# Revit family: Legrand_Lighting_Management_Standalone_Presence_Sensor_Ceiling_R2
name_source: partatom
category: Dispositifs d'éclairage
units: mm (PartAtom-declared; Revit-internal decimal feet)

## family parameters
Conserver l'orientation des annotations = Non
Cote de connecteur circulaire = Utiliser le diamètre
Couper avec des vides une fois chargée = Non
Hôte = Face
Partagée = Non
Point de calcul de pièce = Non
Type d'élément = Normal

## types (16) — shared parameters
COULOIR_PIR = INTERDETECTEUR_COULOIR_PIR
Color = White
Constant light control = Oui
DOUBLE_TECHNO = INTERDETECTEUR_DOUBLE-TECHNO_RACC_VIS
Elévation par défaut = 1219 mm
FAUX_PLAFOND_PIR = DETECTEUR_FAUX_PLAFOND_PIR
Fabricant = LEGRAND
General Conditions of Use = https://export.legrand.com
IP55 = ECODETECTEUR_IP55_ECO_2_GRANDE_HAUTEUR
IR_360 = INTERDETECTEUR_IR_360
IR_360_45_M_2 = INTERDETECTEUR_IR_360_45_M_2
Installation method = Fluxh-mounting
MW_FAUX_PLAFOND = DETECTEUR_MW_FAUX_PLAFOND
PIR_COMPACT = DETECTEUR_PIR_COMPACT
PIR_MID_RANGE = DETECTEUR_PIR_MID_RANGE
PIR_MINI = DETECTEUR_PIR_MINI
Response value luminosity adjustable = Oui
Response value sensitivity adjustable = Oui
URL = www.legrand.fr

## per-type parameters (varying)
- MID RANGE-IR - 360° - 1-10V: DETECTEUR=DETECTEUR_PIR_MID_RANGE; Depth=77 mm  [stored 0.252625 ft]; Detection angle horizontal=360-360 °; Diameter=76 mm  [stored 0.249344 ft]; Diameter detection range on floor=15000 mm  [stored 49.2126 ft]; Frequency=50 Hz; HVAC-control=Non; Height=0 mm  [stored 0 ft]; IK=05; IP=40; Max. duty cycle=99; Max. starting current=80 A; Max. switching power=2300 W; Max. transmission range frontally=7500 mm  [stored 24.6063 ft]; Max. transmission range sideways=7500 mm  [stored 24.6063 ft]; Min. switch-on time=0.5; Operating temperature MIN-MAX=-10/+30 °C; Optimum mounting height=2800 mm  [stored 9.18635 ft]; PETITE_ZONE=Non; Power supply=230 AC; Product Model=presence sensor; Product designation=DETECTOR PIR MID RANGE DIMMING 1-10V & SWITCHING; Reference=LG-048969; Remote operation=Oui; Response value luminosity=0-2000 lx; Sensor type=infrared; Substation input=Oui; Suitable for wireless transmission=Non; Width=76 mm  [stored 0.249344 ft]; With alarm function=Non; With remote control=Oui
- MID RANGE-IR - 360° - DALI: DETECTEUR=DETECTEUR_PIR_MID_RANGE; Depth=77 mm  [stored 0.252625 ft]; Detection angle horizontal=360-360 °; Diameter=76 mm  [stored 0.249344 ft]; Diameter detection range on floor=15000 mm  [stored 49.2126 ft]; Frequency=50 Hz; HVAC-control=Non; Height=0 mm  [stored 0 ft]; IK=05; IP=40; Max. duty cycle=99; Max. starting current=80 A; Max. switching power=2300 W; Max. transmission range frontally=7500 mm  [stored 24.6063 ft]; Max. transmission range sideways=7500 mm  [stored 24.6063 ft]; Min. switch-on time=0.5; Operating temperature MIN-MAX=-10/+30 °C; Optimum mounting height=2800 mm  [stored 9.18635 ft]; PETITE_ZONE=Non; Power supply=230 AC; Product Model=presence sensor; Product designation=DETECTOR PIR MID RANGE DIMMING DALI & SWITCHING; Reference=LG-048968; Remote operation=Oui; Response value luminosity=0-2000 lx; Sensor type=infrared; Substation input=Oui; Suitable for wireless transmission=Non; Width=76 mm  [stored 0.249344 ft]; With alarm function=Non; With remote control=Oui
- MID RANGE-IR - 360° - 2 Chanels: DETECTEUR=DETECTEUR_PIR_MID_RANGE; Depth=70 mm; Detection angle horizontal=360-360 °; Diameter=76 mm  [stored 0.249344 ft]; Diameter detection range on floor=15000 mm  [stored 49.2126 ft]; Frequency=50 Hz; HVAC-control=Non; Height=0 mm  [stored 0 ft]; IK=05; IP=40; Max. duty cycle=99; Max. starting current=80 A; Max. switching power=1300 W; Max. transmission range frontally=7500 mm  [stored 24.6063 ft]; Max. transmission range sideways=7500 mm  [stored 24.6063 ft]; Min. switch-on time=0.5; Operating temperature MIN-MAX=-10/+30 °C; Optimum mounting height=2800 mm  [stored 9.18635 ft]; PETITE_ZONE=Non; Power supply=230 AC; Product Model=presence sensor; Product designation=DETECTOR PIR MID RANGE SWITCHING 2 CHANNELS; Reference=LG-048970; Remote operation=Oui; Response value luminosity=0-2000 lx; Sensor type=infrared; Substation input=Oui; Suitable for wireless transmission=Non; Width=76 mm  [stored 0.249344 ft]; With alarm function=Non; With remote control=Oui
- MINI-IR - 360° - 1-10V: DETECTEUR=DETECTEUR_PIR_MINI; Depth=30 mm  [stored 0.0984252 ft]; Detection angle horizontal=360-360 °; Diameter=28 mm  [stored 0.0918635 ft]; Diameter detection range on floor=7000 mm  [stored 22.9659 ft]; Frequency=50 Hz; HVAC-control=Non; Height=0 mm  [stored 0 ft]; IK=05; IP=40; Max. duty cycle=99; Max. starting current=80 A; Max. switching power=1300 W; Max. transmission range frontally=3500 mm  [stored 11.4829 ft]; Max. transmission range sideways=3500 mm  [stored 11.4829 ft]; Min. switch-on time=0.5; Operating temperature MIN-MAX=-10/+30 °C; Optimum mounting height=2800 mm  [stored 9.18635 ft]; PETITE_ZONE=Oui; Power supply=230 AC; Product Model=presence sensor; Product designation=DETECTOR PIR MINIATURE DIMMING 1-10V & SWITCHING; Reference=LG-048966; Remote operation=Oui; Response value luminosity=0-2000 lx; Sensor type=infrared; Substation input=Oui; Suitable for wireless transmission=Non; Width=76 mm  [stored 0.249344 ft]; With alarm function=Non; With remote control=Oui
- MINI-IR - 360° - DALI: DETECTEUR=DETECTEUR_PIR_MINI; Depth=30 mm  [stored 0.0984252 ft]; Detection angle horizontal=360-360 °; Diameter=0 mm  [stored 0 ft]; Diameter detection range on floor=7000 mm  [stored 22.9659 ft]; Frequency=50 Hz; HVAC-control=Non; Height=33 mm  [stored 0.108268 ft]; IK=05; IP=40; Max. duty cycle=0.1; Max. starting current=80 A; Max. switching power=2400 W; Max. transmission range frontally=7000 mm  [stored 22.9659 ft]; Max. transmission range sideways=7000 mm  [stored 22.9659 ft]; Min. switch-on time=1; Operating temperature MIN-MAX=-10/+35 °C; Optimum mounting height=2800 mm  [stored 9.18635 ft]; PETITE_ZONE=Non; Power supply=230 AC; Product Model=other; Product designation=PIR MINI FALSE CEILING SENSOR DALI DIMMING; Reference=LG-048953; Remote operation=Oui; Response value luminosity=0-2000 lx; Sensor type=infrared; Substation input=Oui; Suitable for wireless transmission=Non; Width=28 mm  [stored 0.0918635 ft]; With alarm function=Non; With remote control=Oui
- MINI-IR - 360° - ON-OFF: DETECTEUR=DETECTEUR_PIR_MINI; Depth=30 mm  [stored 0.0984252 ft]; Detection angle horizontal=360-360 °; Diameter=0 mm  [stored 0 ft]; Diameter detection range on floor=7000 mm  [stored 22.9659 ft]; Frequency=50 Hz; HVAC-control=Non; Height=33 mm  [stored 0.108268 ft]; IK=05; IP=40; Max. duty cycle=0.1; Max. starting current=80 A; Max. switching power=2400 W; Max. transmission range frontally=7000 mm  [stored 22.9659 ft]; Max. transmission range sideways=7000 mm  [stored 22.9659 ft]; Min. switch-on time=1; Operating temperature MIN-MAX=-10/+35 °C; Optimum mounting height=2800 mm  [stored 9.18635 ft]; PETITE_ZONE=Non; Power supply=230 AC; Product Model=other; Product designation=PIR MINI FALSE CEILING SENSOR ON-OFF; Reference=LG-048954; Remote operation=Oui; Response value luminosity=0-2000 lx; Sensor type=infrared; Substation input=Oui; Suitable for wireless transmission=Non; Width=28 mm  [stored 0.0918635 ft]; With alarm function=Non; With remote control=Oui
- COMPACT-IR - 360° - 12-48V: DETECTEUR=DETECTEUR_PIR_COMPACT; Depth=70 mm; Detection angle horizontal=360-360 °; Diameter=0 mm  [stored 0 ft]; Diameter detection range on floor=7000 mm  [stored 22.9659 ft]; Frequency=50 Hz; HVAC-control=Non; Height=65 mm  [stored 0.213255 ft]; IK=05; IP=40; Max. duty cycle=0.1; Max. starting current=80 A; Max. switching power=2400 W; Max. transmission range frontally=7000 mm  [stored 22.9659 ft]; Max. transmission range sideways=7000 mm  [stored 22.9659 ft]; Min. switch-on time=1; Operating temperature MIN-MAX=-10/+35 °C; Optimum mounting height=2800 mm  [stored 9.18635 ft]; PETITE_ZONE=Non; Power supply=24 AC/DC; Product Model=other; Product designation=PIR FALSE CEILING SENSOR LOW VOLTAGE 12-48V SUPPLIED; Reference=LG-048952; Remote operation=Oui; Response value luminosity=0-2000 lx; Sensor type=infrared; Substation input=Oui; Suitable for wireless transmission=Non; Width=76 mm  [stored 0.249344 ft]; With alarm function=Non; With remote control=Oui
- COMPACT-IR - 360° - DALI: DETECTEUR=DETECTEUR_PIR_COMPACT; Depth=70 mm; Detection angle horizontal=360-360 °; Diameter=76 mm  [stored 0.249344 ft]; Diameter detection range on floor=7000 mm  [stored 22.9659 ft]; Frequency=50 Hz; HVAC-control=Non; Height=0 mm  [stored 0 ft]; IK=05; IP=40; Max. duty cycle=99; Max. starting current=80 A; Max. switching power=2300 W; Max. transmission range frontally=3500 mm  [stored 11.4829 ft]; Max. transmission range sideways=3500 mm  [stored 11.4829 ft]; Min. switch-on time=0.5; Operating temperature MIN-MAX=-10/+30 °C; Optimum mounting height=2800 mm  [stored 9.18635 ft]; PETITE_ZONE=Oui; Power supply=230 AC; Product Model=presence sensor; Product designation=DETECTOR PIR COMPACT DIMMING DALI & SWITCHING; Reference=LG-048964; Remote operation=Oui; Response value luminosity=0-2000 lx; Sensor type=infrared; Substation input=Oui; Suitable for wireless transmission=Non; Width=76 mm  [stored 0.249344 ft]; With alarm function=Non; With remote control=Oui
- COMPACT-IR - 360° - 1-10V: DETECTEUR=DETECTEUR_PIR_COMPACT; Depth=70 mm; Detection angle horizontal=360-360 °; Diameter=20 mm  [stored 0.0656168 ft]; Diameter detection range on floor=7000 mm  [stored 22.9659 ft]; Frequency=50 Hz; HVAC-control=Non; Height=0 mm  [stored 0 ft]; IK=05; IP=40; Max. duty cycle=99; Max. starting current=80 A; Max. switching power=2300 W; Max. transmission range frontally=3500 mm  [stored 11.4829 ft]; Max. transmission range sideways=3500 mm  [stored 11.4829 ft]; Min. switch-on time=0.5; Operating temperature MIN-MAX=-10/+30 °C; Optimum mounting height=2800 mm  [stored 9.18635 ft]; PETITE_ZONE=Oui; Power supply=230 AC; Product Model=presence sensor; Product designation=DETECTOR PIR COMPACT DIMMING 1-10V & SWITCHING; Reference=LG-048965; Remote operation=Oui; Response value luminosity=0-2000 lx; Sensor type=infrared; Substation input=Oui; Suitable for wireless transmission=Non; Width=76 mm  [stored 0.249344 ft]; With alarm function=Non; With remote control=Oui
- MW-DALI-Adjustable head: DETECTEUR=DETECTEUR_MW_FAUX_PLAFOND; Depth=99 mm  [stored 0.324803 ft]; Detection angle horizontal=180-360 °; Diameter=0 mm  [stored 0 ft]; Diameter detection range on floor=22000 mm  [stored 72.1785 ft]; Frequency=50 Hz; HVAC-control=Non; Height=96 mm; IK=05; IP=40; Max. duty cycle=0.1; Max. starting current=80 A; Max. switching power=2400 W; Max. transmission range frontally=30000 mm  [stored 98.4252 ft]; Max. transmission range sideways=6000 mm  [stored 19.685 ft]; Min. switch-on time=1; Operating temperature MIN-MAX=-10/+35 °C; Optimum mounting height=2600 mm  [stored 8.53018 ft]; PETITE_ZONE=Non; Power supply=230 AC; Product Model=other; Product designation=MW FALSE CEILING SENSOR DALI DIMMING WITH ADJUSTABLE HEAD; Reference=LG-048956; Remote operation=Oui; Response value luminosity=0-2000 lx; Sensor type=high frequency; Substation input=Oui; Suitable for wireless transmission=Non; Width=85 mm  [stored 0.278871 ft]; With alarm function=Non; With remote control=Oui
- IR - For high Bays and Frost areas: DETECTEUR=DETECTEUR_FAUX_PLAFOND_PIR; Depth=112 mm  [stored 0.367454 ft]; Detection angle horizontal=360-360 °; Diameter=0 mm  [stored 0 ft]; Diameter detection range on floor=40000 mm  [stored 131.234 ft]; Frequency=50 Hz; HVAC-control=Non; Height=112 mm  [stored 0.367454 ft]; IK=05; IP=40; Max. duty cycle=0.1; Max. starting current=80 A; Max. switching power=2400 W; Max. transmission range frontally=40000 mm  [stored 131.234 ft]; Max. transmission range sideways=40000 mm  [stored 131.234 ft]; Min. switch-on time=1; Operating temperature MIN-MAX=-30/+35 °C; Optimum mounting height=15000 mm  [stored 49.2126 ft]; PETITE_ZONE=Non; Power supply=230 AC; Product Model=other; Product designation=PIR FALSE CEILING SENSOR FOR HIGH BAYS AND FROST AREAS; Reference=LG-048959; Remote operation=Oui; Response value luminosity=0-2000 lx; Sensor type=infrared; Substation input=Oui; Suitable for wireless transmission=Non; Width=88 mm  [stored 0.288714 ft]; With alarm function=Non; With remote control=Oui
- ECO2 IP55 Great Hight: DETECTEUR=ECODETECTEUR_IP55_ECO_2_GRANDE_HAUTEUR; Depth=86 mm  [stored 0.282152 ft]; Detection angle horizontal=360-360 °; Diameter=122 mm  [stored 0.400262 ft]; Diameter detection range on floor=25000 mm  [stored 82.021 ft]; Frequency=50-60 Hz; HVAC-control=Non; Height=0 mm  [stored 0 ft]; IK=04; IP=55; Max. duty cycle=60; Max. starting current=8.5 A; Max. switching power=2000 W; Max. transmission range frontally=25000 mm  [stored 82.021 ft]; Max. transmission range sideways=25000 mm  [stored 82.021 ft]; Min. switch-on time=5; Operating temperature MIN-MAX=-25/+45 °C; Optimum mounting height=10000 mm  [stored 32.8084 ft]; PETITE_ZONE=Non; Power supply=230 AC; Product Model=presence sensor; Product designation=Lighting management-traffic detection-surface mounting- IR - 360°- Ø25m; Reference=LG-048932; Remote operation=Oui; Response value luminosity=5-1275 lx; Sensor type=infrared; Substation input=Non; Suitable for wireless transmission=Oui; Width=0 mm  [stored 0 ft]; With alarm function=Non; With remote control=Non
- Corridor PIR: DETECTEUR=INTERDETECTEUR_COULOIR_PIR; Depth=93 mm  [stored 0.305118 ft]; Detection angle horizontal=0-360 °; Diameter=122 mm  [stored 0.400262 ft]; Diameter detection range on floor=24000 mm  [stored 78.7402 ft]; Frequency=50-60 Hz; HVAC-control=Non; Height=0 mm  [stored 0 ft]; IK=04; IP=20; Max. duty cycle=59; Max. starting current=8.5 A; Max. switching power=2000 W; Max. transmission range frontally=3000 mm  [stored 9.84252 ft]; Max. transmission range sideways=12000 mm  [stored 39.3701 ft]; Min. switch-on time=5; Operating temperature MIN-MAX=-5/+45 °C; Optimum mounting height=2500 mm  [stored 8.2021 ft]; PETITE_ZONE=Non; Power supply=230 AC; Product Model=Movement sensor; Product designation=360° ceiling sensor - 90m² - PIR technology - 8.5 A - 240 V - fast connection; Reference=LG-048817; Remote operation=Non; Response value luminosity=5-1275 lx; Sensor type=infrared; Substation input=Oui; Suitable for wireless transmission=Non; Width=0 mm  [stored 0 ft]; With alarm function=Oui; With remote control=Oui
- Dual-tech - Screw mount - 360° - 90m²: DETECTEUR=INTERDETECTEUR_DOUBLE-TECHNO_RACC_VIS; Depth=82 mm  [stored 0.269029 ft]; Detection angle horizontal=0-360 °; Diameter=122 mm  [stored 0.400262 ft]; Diameter detection range on floor=8000 mm  [stored 26.2467 ft]; Frequency=50-60 Hz; HVAC-control=Non; Height=0 mm  [stored 0 ft]; IK=04; IP=20; Max. duty cycle=59; Max. starting current=8.5 A; Max. switching power=2000 W; Max. transmission range frontally=6000 mm  [stored 19.685 ft]; Max. transmission range sideways=4000 mm  [stored 13.1234 ft]; Min. switch-on time=5; Operating temperature MIN-MAX=-5/+45 °C; Optimum mounting height=2500 mm  [stored 8.2021 ft]; PETITE_ZONE=Non; Power supply=230 AC; Product Model=presence sensor; Product designation=Lighting management-digital passage detection-ceiling mounting-DT-90 m² areas; Reference=LG-048806; Remote operation=Oui; Response value luminosity=5-1275 lx; Sensor type=Infrared and ultrasonic; Substation input=Oui; Suitable for wireless transmission=Non; Width=0 mm  [stored 0 ft]; With alarm function=Oui; With remote control=Non
- IR - 360°: DETECTEUR=INTERDETECTEUR_IR_360; Depth=73 mm  [stored 0.239501 ft]; Detection angle horizontal=0-360 °; Diameter=105 mm  [stored 0.344488 ft]; Diameter detection range on floor=8000 mm  [stored 26.2467 ft]; Frequency=50-60 Hz; HVAC-control=Oui; Height=0 mm  [stored 0 ft]; IK=04; IP=20; Max. duty cycle=59; Max. starting current=8.5 A; Max. switching power=2000 W; Max. transmission range frontally=6000 mm  [stored 19.685 ft]; Max. transmission range sideways=4000 mm  [stored 13.1234 ft]; Min. switch-on time=5; Operating temperature MIN-MAX=-5/+45 °C; Optimum mounting height=2500 mm  [stored 8.2021 ft]; PETITE_ZONE=Non; Power supply=230 AC; Product Model=Movement sensor; Product designation=360° switch sensor Mosaic - PIR - Ø 8 m - with 2 A contact for HVAC-  white; Reference=LG-048804; Remote operation=Oui; Response value luminosity=5-1275 lx; Sensor type=infrared; Substation input=Oui; Suitable for wireless transmission=Non; Width=0 mm  [stored 0 ft]; With alarm function=Oui; With remote control=Non
- IR - 360° - 45m²: DETECTEUR=INTERDETECTEUR_IR_360_45_M_2; Depth=82 mm  [stored 0.269029 ft]; Detection angle horizontal=0-360 °; Diameter=102 mm; Diameter detection range on floor=8000 mm  [stored 26.2467 ft]; Frequency=50-60 Hz; HVAC-control=Non; Height=0 mm  [stored 0 ft]; IK=04; IP=20; Max. duty cycle=59; Max. starting current=8.5 A; Max. switching power=2000 W; Max. transmission range frontally=6000 mm  [stored 19.685 ft]; Max. transmission range sideways=4000 mm  [stored 13.1234 ft]; Min. switch-on time=5; Operating temperature MIN-MAX=-5/+45 °C; Optimum mounting height=2500 mm  [stored 8.2021 ft]; PETITE_ZONE=Non; Power supply=230 AC; Product Model=Movement sensor; Product designation=Lighting management-digital passage detection-ceiling mounting-IR-360°-45m²; Reference=LG-048807; Remote operation=Oui; Response value luminosity=5-1275 lx; Sensor type=infrared; Substation input=Oui; Suitable for wireless transmission=Non; Width=0 mm  [stored 0 ft]; With alarm function=Oui; With remote control=Non

note: [stored X ft] marks values corroborated as IEEE doubles in the binary element streams (Revit-internal decimal feet)
